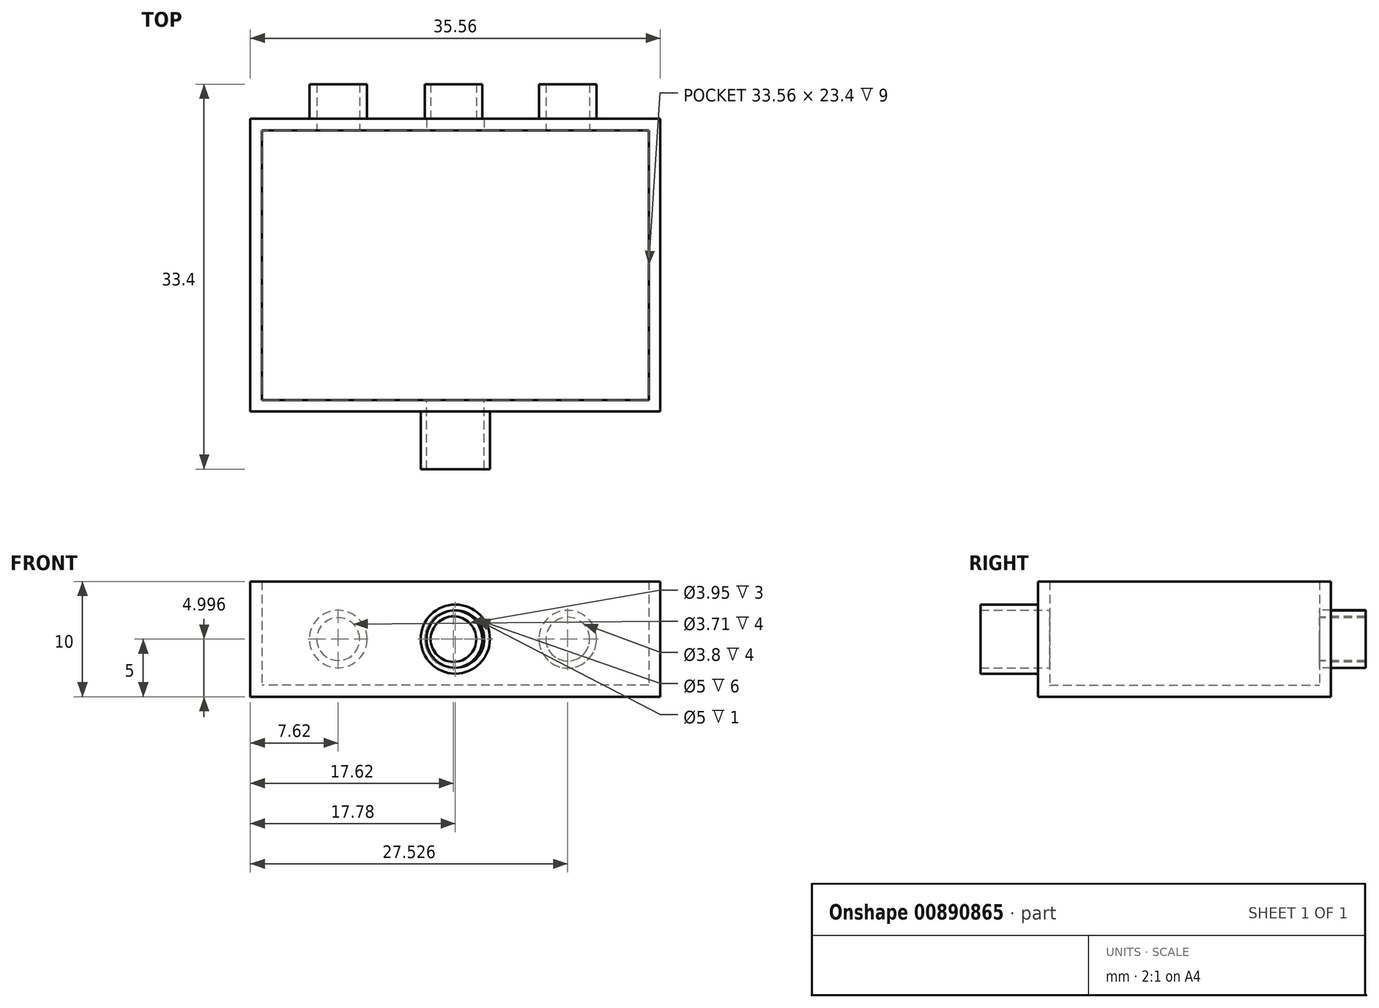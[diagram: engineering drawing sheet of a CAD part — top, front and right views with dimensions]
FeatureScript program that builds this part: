
annotation { "Feature Type Name" : "Feature", "Feature Type Description" : "" }
export const myFeature = defineFeature(function(context is Context, id is Id, definition is map)
    precondition{}
    {
        {
            var Q0;
            Q0=qCreatedBy(makeId("Top.planeOp"),FACE);
            var sketch = newSketch(context, id + "F0", { "sketchPlane" : qUnion([Q0])});
            skLineSegment(sketch, "E0.bottom", {"start": v(0, 4.28) * mm, "end": v(-35.56, 4.28) * mm});
            skLineSegment(sketch, "E0.top", {"start": v(0, 29.68) * mm, "end": v(-35.56, 29.68) * mm});
            skLineSegment(sketch, "E0.left", {"start": v(0, 4.28) * mm, "end": v(0, 29.68) * mm});
            skLineSegment(sketch, "E0.right", {"start": v(-35.56, 4.28) * mm, "end": v(-35.56, 29.68) * mm});
            skPoint(sketch, "E0.middle", {"position": v(-17.78, 16.98) * mm});
            skSolve(sketch);
        }
        {
            var Q0;
            Q0 = qSketchRegion(id + "F0", true);
            extrude(context, id + "F1", {"entities" : qUnion([Q0]), "depth" : 10 * mm, "offsetDistance" : 25.4 * mm});
        }
        {
            var Q0;
            Q0=makeQuery(id+"F1.opExtrude","SWEPT_FACE",FACE,{"disambiguationData":[OSD([sQuery(id+"F0.wireOp",EDGE,"E0.top")])]});
            var sketch = newSketch(context, id + "F2", { "sketchPlane" : qUnion([Q0])});
            skCircle(sketch, "E1", {"center": v(27.94, 5) * mm, "radius": 2.5 * mm});
            skCircle(sketch, "E2", {"center": v(17.94, 5) * mm, "radius": 2.5 * mm});
            skCircle(sketch, "E3", {"center": v(8.03, 5) * mm, "radius": 2.5 * mm});
            skCircle(sketch, "E4", {"center": v(8.03, 5) * mm, "radius": 1.9 * mm});
            skCircle(sketch, "E5", {"center": v(17.94, 5) * mm, "radius": 1.98 * mm});
            skCircle(sketch, "E6", {"center": v(27.94, 5) * mm, "radius": 1.86 * mm});
            skSolve(sketch);
        }
        {
            var Q0;
            Q0=makeQuery(id+"F1.opExtrude","CAP_FACE",FACE,{"disambiguationData":[OSD([sQuery(id+"F0.wireOp",EDGE,"E0.bottom"),sQuery(id+"F0.wireOp",EDGE,"E0.top"),sQuery(id+"F0.wireOp",EDGE,"E0.left"),sQuery(id+"F0.wireOp",EDGE,"E0.right")])],"isStart":false});
            shell(context, id + "F3", {"entities" : qUnion([Q0]), "thickness" : 1 * mm});
        }
        {
            var Q0;
            Q0=makeQuery(id+"F2.imprint","IMPRINT",FACE,{"disambiguationData":[TD([[makeQuery(id+"F2.imprint","IMPRINT",EDGE,{"derivedFrom":sQuery(id+"F2.wireOp",EDGE,"E1")}),1.0]])]});
            var Q1;
            Q1=makeQuery(id+"F2.imprint","IMPRINT",FACE,{"disambiguationData":[TD([[makeQuery(id+"F2.imprint","IMPRINT",EDGE,{"derivedFrom":sQuery(id+"F2.wireOp",EDGE,"E2")}),1.0]])]});
            var Q2;
            Q2=makeQuery(id+"F2.imprint","IMPRINT",FACE,{"disambiguationData":[TD([[makeQuery(id+"F2.imprint","IMPRINT",EDGE,{"derivedFrom":sQuery(id+"F2.wireOp",EDGE,"E3")}),1.0]])]});
            extrude(context, id + "F4", {"entities" : qUnion([Q0, Q1, Q2]), "operationType" : NewBodyOperationType.ADD, "depth" : 3 * mm, "offsetDistance" : 25.4 * mm});
        }
        {
            var Q0;
            Q0=makeQuery(id+"F4.boolean.opBoolean","SPLIT",FACE,{"disambiguationData":[TD([makeQuery(id+"F4.opExtrude","SWEPT_FACE",FACE,{"disambiguationData":[OSD([sQuery(id+"F2.wireOp",EDGE,"E6")])]})])],"derivedFrom":makeQuery(id+"F1.opExtrude","SWEPT_FACE",FACE,{"disambiguationData":[OSD([sQuery(id+"F0.wireOp",EDGE,"E0.top")])]})});
            var Q1;
            Q1=makeQuery(id+"F4.boolean.opBoolean","SPLIT",FACE,{"disambiguationData":[TD([makeQuery(id+"F4.opExtrude","SWEPT_FACE",FACE,{"disambiguationData":[OSD([sQuery(id+"F2.wireOp",EDGE,"E5")])]})])],"derivedFrom":makeQuery(id+"F1.opExtrude","SWEPT_FACE",FACE,{"disambiguationData":[OSD([sQuery(id+"F0.wireOp",EDGE,"E0.top")])]})});
            var Q2;
            Q2=makeQuery(id+"F4.boolean.opBoolean","SPLIT",FACE,{"disambiguationData":[TD([makeQuery(id+"F4.opExtrude","SWEPT_FACE",FACE,{"disambiguationData":[OSD([sQuery(id+"F2.wireOp",EDGE,"E4")])]})])],"derivedFrom":makeQuery(id+"F1.opExtrude","SWEPT_FACE",FACE,{"disambiguationData":[OSD([sQuery(id+"F0.wireOp",EDGE,"E0.top")])]})});
            extrude(context, id + "F5", {"entities" : qUnion([Q0, Q1, Q2]), "operationType" : NewBodyOperationType.REMOVE, "endBound" : BoundingType.UP_TO_NEXT, "oppositeDirection" : true, "depth" : 25.4 * mm, "offsetDistance" : 25.4 * mm});
        }
        {
            var Q0;
            Q0=makeQuery(id+"F1.opExtrude","SWEPT_FACE",FACE,{"disambiguationData":[OSD([sQuery(id+"F0.wireOp",EDGE,"E0.bottom")])]});
            var sketch = newSketch(context, id + "F6", { "sketchPlane" : qUnion([Q0])});
            skCircle(sketch, "E7", {"center": v(-17.78, 5) * mm, "radius": 3 * mm});
            skLineSegment(sketch, "E8", {"start": v(-35.56, 5) * mm, "end": v(0, 5) * mm, "construction": true});
            skCircle(sketch, "E9", {"center": v(-17.78, 5) * mm, "radius": 2.5 * mm});
            skSolve(sketch);
        }
        {
            var Q0;
            Q0 = qSketchRegion(id + "F6", true);
            extrude(context, id + "F7", {"entities" : qUnion([Q0]), "operationType" : NewBodyOperationType.ADD, "depth" : 5 * mm, "offsetDistance" : 25.4 * mm});
        }
        {
            var Q0;
            Q0=makeQuery(id+"F7.boolean.opBoolean","SPLIT",FACE,{"disambiguationData":[TD([makeQuery(id+"F7.opExtrude","SWEPT_FACE",FACE,{"disambiguationData":[OSD([sQuery(id+"F6.wireOp",EDGE,"E9")])]})])],"derivedFrom":makeQuery(id+"F1.opExtrude","SWEPT_FACE",FACE,{"disambiguationData":[OSD([sQuery(id+"F0.wireOp",EDGE,"E0.bottom")])]})});
            extrude(context, id + "F8", {"entities" : qUnion([Q0]), "operationType" : NewBodyOperationType.REMOVE, "oppositeDirection" : true, "depth" : 25.4 * mm, "offsetDistance" : 25.4 * mm});
        }
    });
